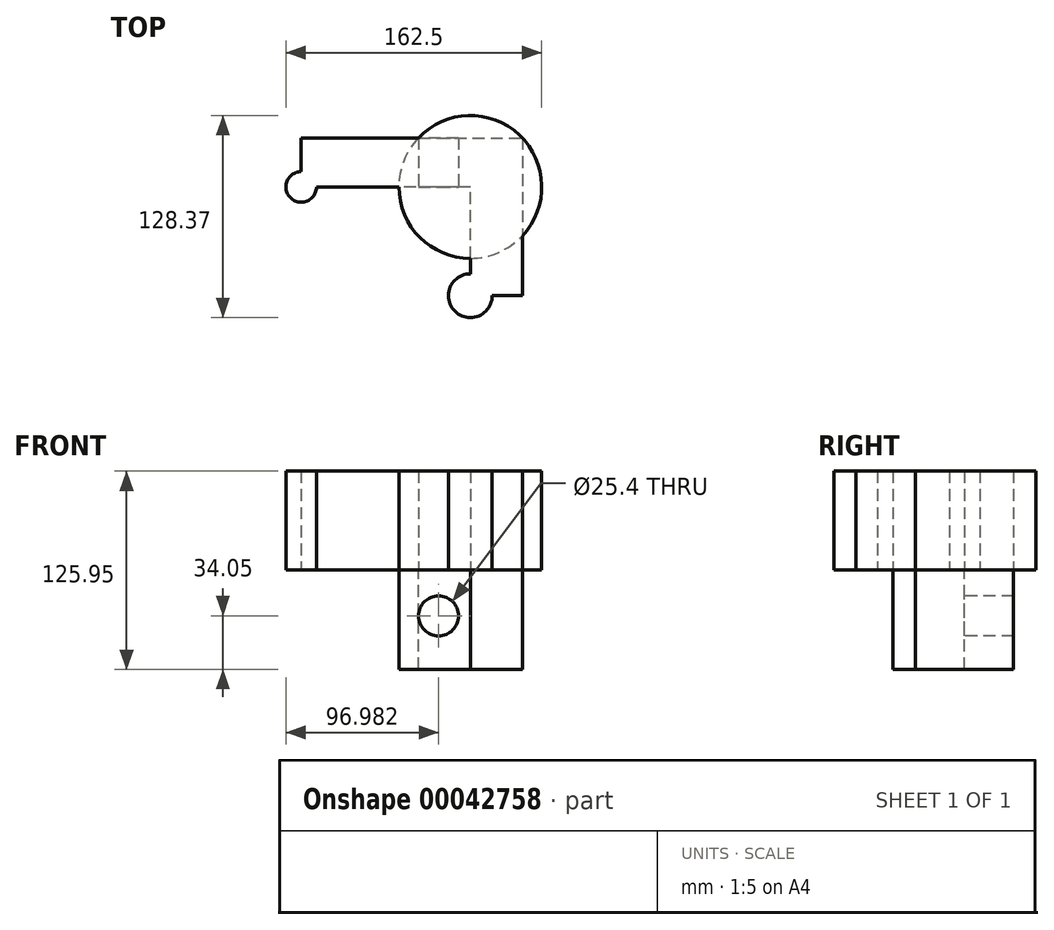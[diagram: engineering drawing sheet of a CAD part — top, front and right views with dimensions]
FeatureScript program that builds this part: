
annotation { "Feature Type Name" : "Feature", "Feature Type Description" : "" }
export const myFeature = defineFeature(function(context is Context, id is Id, definition is map)
    precondition{}
    {
        {
            var Q0;
            Q0=qCreatedBy(makeId("Top.planeOp"),FACE);
            var sketch = newSketch(context, id + "F0", { "sketchPlane" : qUnion([Q0])});
            skLineSegment(sketch, "E0", {"start": v(0, 0) * mm, "end": v(-32.98, 0) * mm});
            skLineSegment(sketch, "E1", {"start": v(-32.98, 0) * mm, "end": v(-32.98, 69.1) * mm});
            skLineSegment(sketch, "E2", {"start": v(-32.98, 69.1) * mm, "end": v(-140.43, 69.1) * mm});
            skLineSegment(sketch, "E3", {"start": v(-140.43, 69.1) * mm, "end": v(-140.43, 100.23) * mm});
            skLineSegment(sketch, "E4", {"start": v(0, 100.23) * mm, "end": v(0, 0) * mm});
            skLineSegment(sketch, "E5", {"start": v(-140.43, 100.23) * mm, "end": v(0, 100.23) * mm});
            skCircle(sketch, "E6", {"center": v(-32.98, 69.1) * mm, "radius": 45.35 * mm});
            skCircle(sketch, "E7", {"center": v(-140.43, 69.1) * mm, "radius": 9.7 * mm});
            skCircle(sketch, "E8", {"center": v(-32.98, 0) * mm, "radius": 13.92 * mm});
            skSolve(sketch);
        }
        {
            var Q0;
            {var subQ0=sQuery(id+"F0.wireOp",EDGE,"E3");var subQ3=sQuery(id+"F0.wireOp",EDGE,"E2");var subQ4=makeQuery(id+"F0.imprint","INTERSECT",VERTEX,{"derivedFrom":[subQ3,subQ0]});Q0=makeQuery(id+"F0.imprint","IMPRINT",FACE,{"disambiguationData":[TD([[makeQuery(id+"F0.imprint","IMPRINT",EDGE,{"disambiguationData":[TD([[subQ4,1.0]])],"derivedFrom":subQ3}),1.0]])]});}
            var Q1;
            {var subQ1=sQuery(id+"F0.wireOp",EDGE,"E1");var subQ3=sQuery(id+"F0.wireOp",EDGE,"E0");var subQ5=makeQuery(id+"F0.imprint","INTERSECT",VERTEX,{"derivedFrom":[subQ3,subQ1]});Q1=makeQuery(id+"F0.imprint","IMPRINT",FACE,{"disambiguationData":[TD([[makeQuery(id+"F0.imprint","IMPRINT",EDGE,{"disambiguationData":[TD([[subQ5,1.0]])],"derivedFrom":subQ3}),1.0]])]});}
            var Q2;
            {var subQ1=sQuery(id+"F0.wireOp",EDGE,"E2");var subQ3=sQuery(id+"F0.wireOp",EDGE,"E1");var subQ5=makeQuery(id+"F0.imprint","INTERSECT",VERTEX,{"derivedFrom":[subQ3,subQ1]});Q2=makeQuery(id+"F0.imprint","IMPRINT",FACE,{"disambiguationData":[TD([[makeQuery(id+"F0.imprint","IMPRINT",EDGE,{"disambiguationData":[TD([[subQ5,1.0]])],"derivedFrom":subQ3}),1.0]])]});}
            var Q3;
            {var subQ0=sQuery(id+"F0.wireOp",EDGE,"E6");var subQ1=sQuery(id+"F0.wireOp",EDGE,"E4");var subQ2=makeQuery(id+"F0.imprint","INTERSECT",VERTEX,{"derivedFrom":[subQ1,subQ0]});Q3=makeQuery(id+"F0.imprint","IMPRINT",FACE,{"disambiguationData":[TD([[makeQuery(id+"F0.imprint","IMPRINT",EDGE,{"disambiguationData":[TD([[subQ2,1.0]])],"derivedFrom":subQ1}),1.0]])]});}
            var Q4;
            {var subQ3=sQuery(id+"F0.wireOp",EDGE,"E0");var subQ5=sQuery(id+"F0.wireOp",EDGE,"E4");var subQ6=makeQuery(id+"F0.imprint","INTERSECT",VERTEX,{"derivedFrom":[subQ3,subQ5]});Q4=makeQuery(id+"F0.imprint","IMPRINT",FACE,{"disambiguationData":[TD([[makeQuery(id+"F0.imprint","IMPRINT",EDGE,{"disambiguationData":[TD([[subQ6,-1.0]])],"derivedFrom":subQ3}),-1.0]])]});}
            var Q5;
            {var subQ1=sQuery(id+"F0.wireOp",EDGE,"E1");var subQ3=sQuery(id+"F0.wireOp",EDGE,"E0");var subQ5=makeQuery(id+"F0.imprint","INTERSECT",VERTEX,{"derivedFrom":[subQ3,subQ1]});Q5=makeQuery(id+"F0.imprint","IMPRINT",FACE,{"disambiguationData":[TD([[makeQuery(id+"F0.imprint","IMPRINT",EDGE,{"disambiguationData":[TD([[subQ5,1.0]])],"derivedFrom":subQ3}),-1.0]])]});}
            var Q6;
            {var subQ3=sQuery(id+"F0.wireOp",EDGE,"E2");var subQ5=sQuery(id+"F0.wireOp",EDGE,"E6");var subQ6=makeQuery(id+"F0.imprint","INTERSECT",VERTEX,{"derivedFrom":[subQ3,subQ5]});Q6=makeQuery(id+"F0.imprint","IMPRINT",FACE,{"disambiguationData":[TD([[makeQuery(id+"F0.imprint","IMPRINT",EDGE,{"disambiguationData":[TD([[subQ6,-1.0]])],"derivedFrom":subQ3}),-1.0]])]});}
            var Q7;
            {var subQ0=sQuery(id+"F0.wireOp",EDGE,"E3");var subQ3=sQuery(id+"F0.wireOp",EDGE,"E2");var subQ4=makeQuery(id+"F0.imprint","INTERSECT",VERTEX,{"derivedFrom":[subQ3,subQ0]});Q7=makeQuery(id+"F0.imprint","IMPRINT",FACE,{"disambiguationData":[TD([[makeQuery(id+"F0.imprint","IMPRINT",EDGE,{"disambiguationData":[TD([[subQ4,1.0]])],"derivedFrom":subQ3}),-1.0]])]});}
            var Q8;
            {var subQ3=sQuery(id+"F0.wireOp",EDGE,"E2");var subQ5=sQuery(id+"F0.wireOp",EDGE,"E1");var subQ7=makeQuery(id+"F0.imprint","INTERSECT",VERTEX,{"derivedFrom":[subQ5,subQ3]});Q8=makeQuery(id+"F0.imprint","IMPRINT",FACE,{"disambiguationData":[TD([[makeQuery(id+"F0.imprint","IMPRINT",EDGE,{"disambiguationData":[TD([[subQ7,1.0]])],"derivedFrom":subQ5}),-1.0]])]});}
            var Q9;
            {var subQ0=sQuery(id+"F0.wireOp",EDGE,"E6");var subQ1=sQuery(id+"F0.wireOp",EDGE,"E5");var subQ2=makeQuery(id+"F0.imprint","INTERSECT",VERTEX,{"derivedFrom":[subQ1,subQ0]});Q9=makeQuery(id+"F0.imprint","IMPRINT",FACE,{"disambiguationData":[TD([[makeQuery(id+"F0.imprint","IMPRINT",EDGE,{"disambiguationData":[TD([[subQ2,-1.0]])],"derivedFrom":subQ1}),1.0]])]});}
            extrude(context, id + "F1", {"entities" : qUnion([Q0, Q1, Q2, Q3, Q4, Q5, Q6, Q7, Q8, Q9]), "depth" : 62.86 * mm});
        }
        {
            var Q0;
            {var subQ3=sQuery(id+"F0.wireOp",EDGE,"E2");var subQ5=sQuery(id+"F0.wireOp",EDGE,"E1");var subQ7=makeQuery(id+"F0.imprint","INTERSECT",VERTEX,{"derivedFrom":[subQ5,subQ3]});Q0=makeQuery(id+"F0.imprint","IMPRINT",FACE,{"disambiguationData":[TD([[makeQuery(id+"F0.imprint","IMPRINT",EDGE,{"disambiguationData":[TD([[subQ7,1.0]])],"derivedFrom":subQ5}),-1.0]])]});}
            extrude(context, id + "F2", {"entities" : qUnion([Q0]), "oppositeDirection" : true, "depth" : 63.1 * mm});
        }
        {
            var Q0;
            Q0=makeQuery(id+"F2.opExtrude","SWEPT_FACE",FACE,{"disambiguationData":[OSD([sQuery(id+"F0.wireOp",EDGE,"E2")])]});
            var sketch = newSketch(context, id + "F3", { "sketchPlane" : qUnion([Q0])});
            skCircle(sketch, "E9", {"center": v(-53.15, -29.04) * mm, "radius": 12.7 * mm});
            skSolve(sketch);
        }
        {
            var Q0;
            Q0=makeQuery(id+"F3.imprint","IMPRINT",FACE,{"disambiguationData":[TD([[makeQuery(id+"F3.imprint","IMPRINT",EDGE,{"derivedFrom":sQuery(id+"F3.wireOp",EDGE,"E9")}),1.0]])]});
            extrude(context, id + "F4", {"entities" : qUnion([Q0]), "operationType" : NewBodyOperationType.REMOVE, "oppositeDirection" : true, "depth" : 54.77 * mm});
        }
    });
